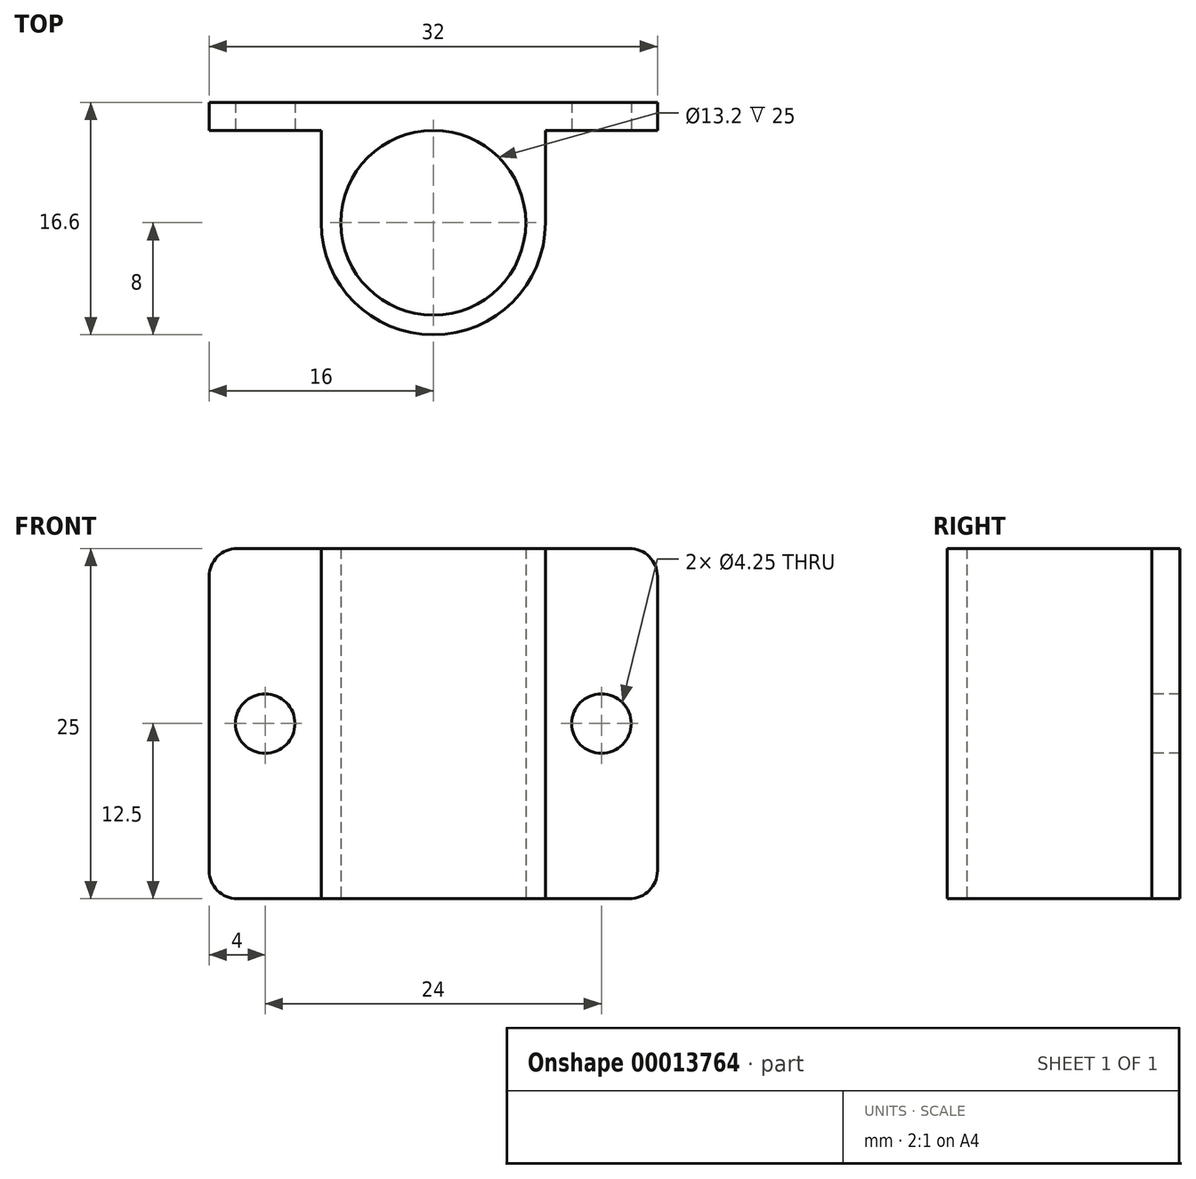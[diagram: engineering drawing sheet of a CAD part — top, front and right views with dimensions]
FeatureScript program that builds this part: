
annotation { "Feature Type Name" : "Feature", "Feature Type Description" : "" }
export const myFeature = defineFeature(function(context is Context, id is Id, definition is map)
    precondition{}
    {
        {
            var Q0;
            Q0=qCreatedBy(makeId("Top.planeOp"),FACE);
            var sketch = newSketch(context, id + "F0", { "sketchPlane" : qUnion([Q0])});
            skCircle(sketch, "E0", {"center": v(0, 0) * mm, "radius": 6.6 * mm});
            skCircle(sketch, "E1", {"center": v(0, 0) * mm, "radius": 8 * mm});
            skLineSegment(sketch, "E2", {"start": v(-16, 8.6) * mm, "end": v(-16, 6.6) * mm});
            skLineSegment(sketch, "E3", {"start": v(-16, 6.6) * mm, "end": v(0, 6.6) * mm});
            skLineSegment(sketch, "E4", {"start": v(-16, 8.6) * mm, "end": v(0, 8.6) * mm});
            skLineSegment(sketch, "E5", {"start": v(-8, 0) * mm, "end": v(-8, 6.6) * mm});
            skLineSegment(sketch, "E6.0.MirrorCS", {"start": v(16, 8.6) * mm, "end": v(0, 8.6) * mm});
            skLineSegment(sketch, "E7.0.MirrorCS", {"start": v(16, 8.6) * mm, "end": v(16, 6.6) * mm});
            skLineSegment(sketch, "E8.0.MirrorCS", {"start": v(16, 6.6) * mm, "end": v(0, 6.6) * mm});
            skLineSegment(sketch, "E9.0.MirrorCS", {"start": v(8, 0) * mm, "end": v(8, 6.6) * mm});
            skSolve(sketch);
        }
        {
            var Q0;
            Q0 = qSketchRegion(id + "F0", true);
            var Q1;
            {var subQ0=sQuery(id+"F0.wireOp",EDGE,"E8.0.MirrorCS");var subQ1=sQuery(id+"F0.wireOp",EDGE,"E1");var subQ2=makeQuery(id+"F0.imprint","INTERSECT",VERTEX,{"derivedFrom":[subQ1,subQ0]});Q1=makeQuery(id+"F0.imprint","IMPRINT",FACE,{"disambiguationData":[TD([[makeQuery(id+"F0.imprint","IMPRINT",EDGE,{"disambiguationData":[TD([[subQ2,-1.0]])],"derivedFrom":subQ1}),1.0]])]});}
            extrude(context, id + "F1", {"entities" : qUnion([Q0, Q1]), "depth" : 25 * mm});
        }
        {
            var Q0;
            Q0=makeQuery(id+"F1.opExtrude","SWEPT_FACE",FACE,{"disambiguationData":[OSD([sQuery(id+"F0.wireOp",EDGE,"E3")])]});
            var sketch = newSketch(context, id + "F2", { "sketchPlane" : qUnion([Q0])});
            skLineSegment(sketch, "E10", {"start": v(-12, 25) * mm, "end": v(-12, 0) * mm, "construction": true});
            skCircle(sketch, "E11", {"center": v(-12, 12.5) * mm, "radius": 2.12 * mm});
            skCircle(sketch, "E12.0.MirrorC", {"center": v(12, 12.5) * mm, "radius": 2.12 * mm});
            skSolve(sketch);
        }
        {
            var Q0;
            Q0 = qSketchRegion(id + "F2", true);
            extrude(context, id + "F3", {"entities" : qUnion([Q0]), "operationType" : NewBodyOperationType.REMOVE, "endBound" : BoundingType.THROUGH_ALL, "oppositeDirection" : true, "depth" : 25 * mm});
        }
        {
            var Q0;
            Q0=makeQuery(id+"F1.opExtrude","CAP_EDGE",EDGE,{"disambiguationData":[OSD([sQuery(id+"F0.wireOp",EDGE,"E2")])],"isStart":false});
            var Q1;
            Q1=makeQuery(id+"F1.opExtrude","CAP_EDGE",EDGE,{"disambiguationData":[OSD([sQuery(id+"F0.wireOp",EDGE,"E2")])],"isStart":true});
            var Q2;
            Q2=makeQuery(id+"F1.opExtrude","CAP_EDGE",EDGE,{"disambiguationData":[OSD([sQuery(id+"F0.wireOp",EDGE,"E7.0.MirrorCS")])],"isStart":true});
            var Q3;
            Q3=makeQuery(id+"F1.opExtrude","CAP_EDGE",EDGE,{"disambiguationData":[OSD([sQuery(id+"F0.wireOp",EDGE,"E7.0.MirrorCS")])],"isStart":false});
            fillet(context, id + "F4", {"entities" : qUnion([Q0, Q1, Q2, Q3]), "radius" : 2 * mm, "tangentPropagation" : true, "allowEdgeOverflow" : false});
        }
    });
